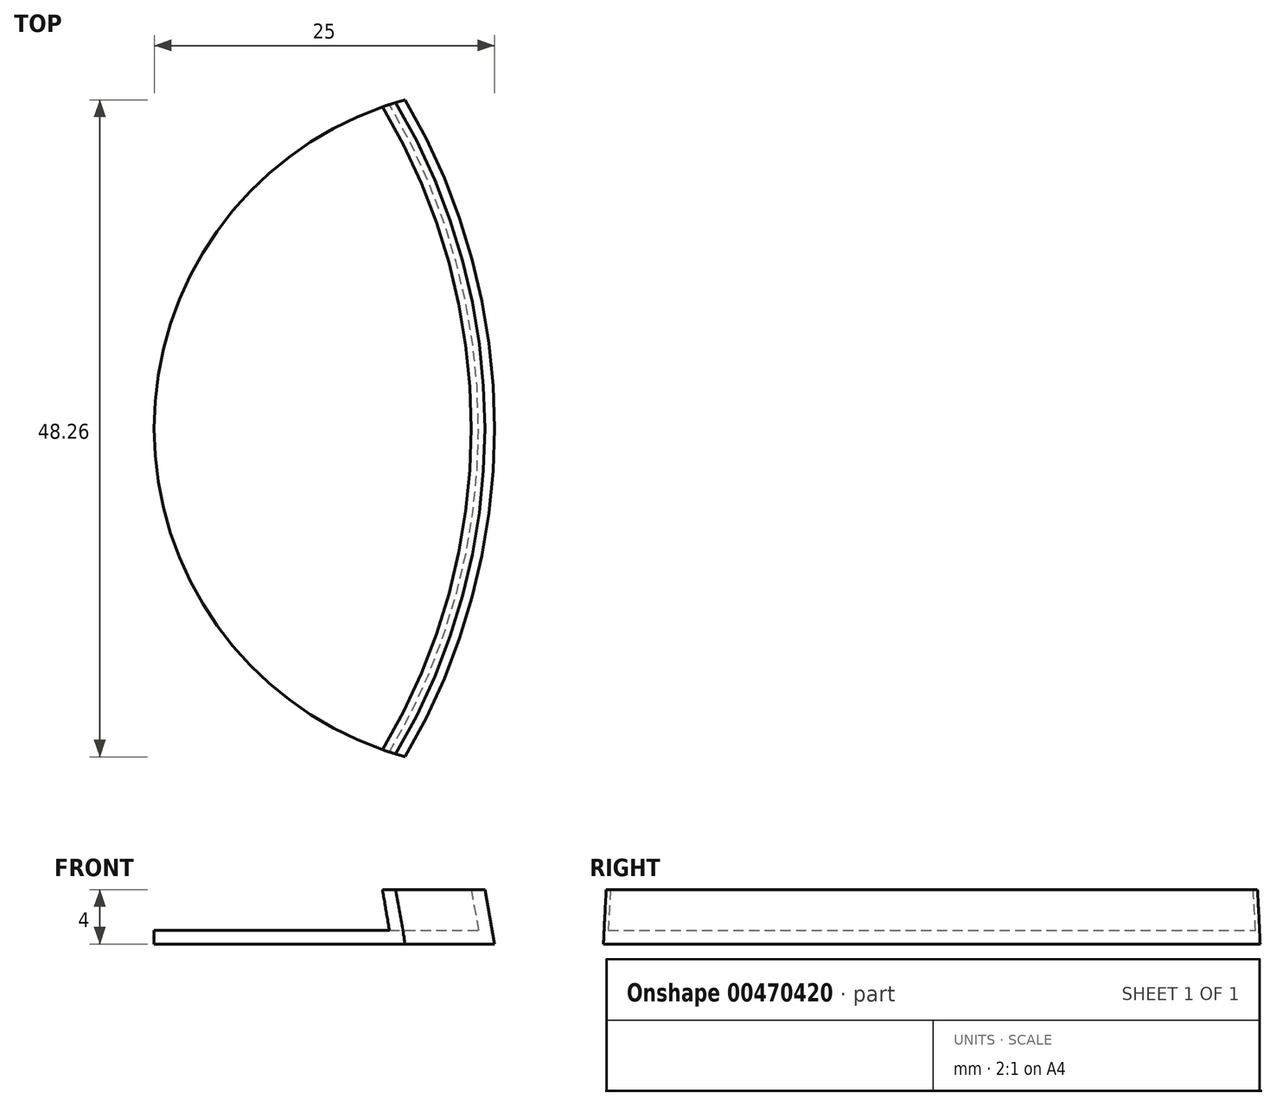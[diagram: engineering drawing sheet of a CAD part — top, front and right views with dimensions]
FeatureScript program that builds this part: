
annotation { "Feature Type Name" : "Feature", "Feature Type Description" : "" }
export const myFeature = defineFeature(function(context is Context, id is Id, definition is map)
    precondition{}
    {
        {
            var Q0;
            Q0=qCreatedBy(makeId("Right.planeOp"),FACE);
            var sketch = newSketch(context, id + "F0", { "sketchPlane" : qUnion([Q0])});
            skLineSegment(sketch, "E0", {"start": v(0, 0) * mm, "end": v(-47.68, 0) * mm});
            skLineSegment(sketch, "E1", {"start": v(-47.68, 0) * mm, "end": v(-46.97, 4) * mm});
            skLineSegment(sketch, "E2", {"start": v(-46.97, 4) * mm, "end": v(-45.97, 4) * mm});
            skLineSegment(sketch, "E3", {"start": v(-45.97, 4) * mm, "end": v(-46.5, 1) * mm});
            skLineSegment(sketch, "E4", {"start": v(-46.5, 1) * mm, "end": v(0, 1) * mm});
            skLineSegment(sketch, "E5", {"start": v(0, 1) * mm, "end": v(0, 0) * mm});
            skSolve(sketch);
        }
        {
            var Q0;
            Q0 = qSketchRegion(id + "F0", true);
            var Q1;
            Q1=sQuery(id+"F0.wireOp",EDGE,"E5");
            revolve(context, id + "F1", {"entities" : qUnion([Q0]), "axis" : qUnion([Q1]), "revolveType" : RevolveType.FULL});
        }
        {
            var Q0;
            Q0=makeQuery(id+"F1.opRevolve","SWEPT_FACE",FACE,{"disambiguationData":[OSD([sQuery(id+"F0.wireOp",EDGE,"E0")])]});
            var sketch = newSketch(context, id + "F2", { "sketchPlane" : qUnion([Q0])});
            skArc(sketch, "E6", {"start": v(-41.12, -24.13) * mm, "mid": v(-22.68, 0) * mm, "end": v(-41.12, 24.13) * mm});
            skLineSegment(sketch, "E7", {"start": v(0, 0) * mm, "end": v(0, 21.17) * mm, "construction": true});
            skPoint(sketch, "E8.end.orphan", {"position": v(0, 35.7) * mm});
            skCircle(sketch, "E9", {"center": v(0, 0) * mm, "radius": 47.68 * mm});
            skArc(sketch, "E10.MirrorCS", {"start": v(41.12, -24.13) * mm, "mid": v(22.68, 0) * mm, "end": v(41.12, 24.13) * mm});
            skSolve(sketch);
        }
        {
            var Q0;
            {var subQ0=sQuery(id+"F2.wireOp",EDGE,"E6");Q0=makeQuery(id+"F2.imprint","IMPRINT",FACE,{"disambiguationData":[TD([[makeQuery(id+"F2.imprint","IMPRINT",EDGE,{"derivedFrom":subQ0}),1.0]])]});}
            var Q1;
            {var subQ0=sQuery(id+"F2.wireOp",EDGE,"E10.MirrorCS");Q1=makeQuery(id+"F2.imprint","IMPRINT",FACE,{"disambiguationData":[TD([[makeQuery(id+"F2.imprint","IMPRINT",EDGE,{"derivedFrom":subQ0}),-1.0]])]});}
            extrude(context, id + "F3", {"entities" : qUnion([Q0, Q1]), "operationType" : NewBodyOperationType.REMOVE, "endBound" : BoundingType.THROUGH_ALL, "oppositeDirection" : true, "depth" : 25 * mm});
        }
    });
